# Revit family: Sink-Double_Bowl-American_Standard-Fairbury_2S-18DB000332C1_Series
name_source: partatom
category: Plumbing Fixtures
units: mm (PartAtom-declared; Revit-internal decimal feet)

## family parameters
Always vertical = No
Cut with Voids When Loaded = No
OmniClass Number = 23.45.05.14.14
OmniClass Title = Sinks/Lavatories
Part Type = Normal
Room Calculation Point = No
Round Connector Dimension = Use Diameter
Shared = Yes
Work Plane-Based = Yes

## types (1)
- 18DB000332C1.075
    7418300 Pull Down Faucet = Yes
    9028000.075 Waste Fittings = Yes
    ADA Compliant = Yes
    Assembly Code = D2010410
    Basin Shape = Rectangular
    Bowl Length = 19 7/16"
    Bowl Width = 14 9/16"
    CW Connection = Yes
    CWFU = 2
    Cold Water Connection Diameter = 3/8"
    Compliance Certifications = ASME A112.19.3, CSA B45.4
    Default Elevation = 9"
    Description = Fairbury® 2S Pull-Down Faucet and 33-Inch Stainless Steel Double-Bowl Kitchen Sink Kit
    Finish = Metal-American Standard-075-Stainless Steel
    HW Connection = Yes
    HWFU = 2
    Height = 9"
    Hot Water Connection Diameter = 0"
    Installation Type = Dual mount design – Can be installed above or below the countertop
    Length = 33"
    Manufacturer = American Standard
    Material = Metal-American Standard-075-Stainless Steel
    Model = 18DB000332C1.075
    Pipe Height From Sink Bottom = 1"
    Product Documentation Link = https://lixil.cdn.celum.cloud
    Product Page URL = https://www.americanstandard-us.com
    Revised Date = 05/22/2024
    Sink Distance to the Wall = 2 1/2"
    Soap Dispenser = Yes
    URL = https://www.americanstandard-us.com
    Vent Connection = No
    WFU = 3
    Warranty Information = Limited Lifetime Warranty
    Waste Connection = Yes
    Waste Connection Diameter = 1 1/4"
    Width = 22"

## geometry (parser evidence)
native form markers: Sweep x6
no freeform markers — native parametric forms only
